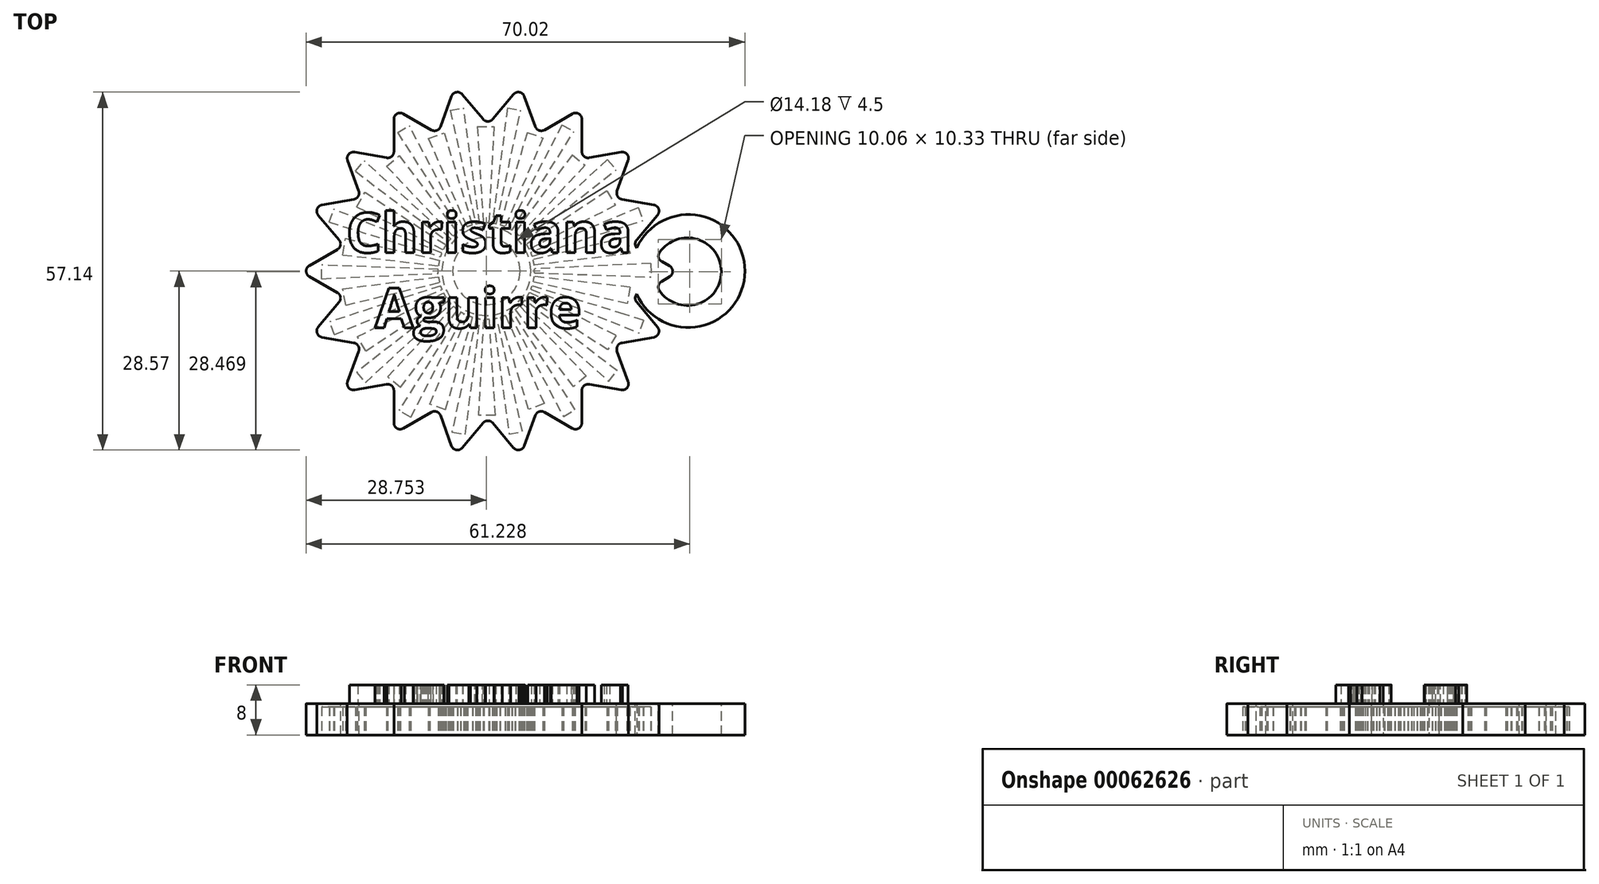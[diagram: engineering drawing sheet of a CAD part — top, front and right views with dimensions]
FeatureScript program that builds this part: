
annotation { "Feature Type Name" : "Feature", "Feature Type Description" : "" }
export const myFeature = defineFeature(function(context is Context, id is Id, definition is map)
    precondition{}
    {
        {
            var Q0;
            Q0=qCreatedBy(makeId("Top.planeOp"),FACE);
            var sketch = newSketch(context, id + "F0", { "sketchPlane" : qUnion([Q0])});
            skLineSegment(sketch, "E0", {"start": v(-64.22, 4.05) * mm, "end": v(-69.43, 10.26) * mm});
            skLineSegment(sketch, "E1", {"start": v(-69.43, 10.26) * mm, "end": v(-61.45, 11.67) * mm});
            skCircle(sketch, "E2.0", {"center": v(-41.24, 0) * mm, "radius": 30 * mm, "construction": true});
            skLineSegment(sketch, "E3", {"start": v(-61.45, 11.67) * mm, "end": v(-64.22, 19.28) * mm});
            skLineSegment(sketch, "E4", {"start": v(-64.22, 19.28) * mm, "end": v(-56.24, 17.88) * mm});
            skLineSegment(sketch, "E5", {"start": v(-56.24, 17.88) * mm, "end": v(-56.24, 25.98) * mm});
            skLineSegment(sketch, "E6", {"start": v(-56.24, 25.98) * mm, "end": v(-49.22, 21.93) * mm});
            skLineSegment(sketch, "E7", {"start": v(-49.22, 21.93) * mm, "end": v(-46.45, 29.54) * mm});
            skLineSegment(sketch, "E8", {"start": v(-46.45, 29.54) * mm, "end": v(-41.24, 23.34) * mm});
            skLineSegment(sketch, "E9", {"start": v(-41.24, 23.34) * mm, "end": v(-36.03, 29.54) * mm});
            skLineSegment(sketch, "E10", {"start": v(-36.03, 29.54) * mm, "end": v(-33.26, 21.93) * mm});
            skLineSegment(sketch, "E11", {"start": v(-33.26, 21.93) * mm, "end": v(-26.24, 25.98) * mm});
            skLineSegment(sketch, "E12", {"start": v(-26.24, 25.98) * mm, "end": v(-26.24, 17.88) * mm});
            skLineSegment(sketch, "E13", {"start": v(-26.24, 17.88) * mm, "end": v(-18.26, 19.28) * mm});
            skLineSegment(sketch, "E14", {"start": v(-18.26, 19.28) * mm, "end": v(-21.03, 11.67) * mm});
            skLineSegment(sketch, "E15", {"start": v(-21.03, 11.67) * mm, "end": v(-13.05, 10.26) * mm});
            skLineSegment(sketch, "E16", {"start": v(-13.05, 10.26) * mm, "end": v(-18.26, 4.05) * mm});
            skLineSegment(sketch, "E17", {"start": v(-18.26, 4.05) * mm, "end": v(-11.24, 0) * mm});
            skLineSegment(sketch, "E18", {"start": v(-11.24, 0) * mm, "end": v(-18.26, -4.05) * mm});
            skLineSegment(sketch, "E19", {"start": v(-18.26, -4.05) * mm, "end": v(-13.05, -10.26) * mm});
            skLineSegment(sketch, "E20", {"start": v(-13.05, -10.26) * mm, "end": v(-21.03, -11.67) * mm});
            skLineSegment(sketch, "E21", {"start": v(-21.03, -11.67) * mm, "end": v(-18.26, -19.28) * mm});
            skLineSegment(sketch, "E22", {"start": v(-18.26, -19.28) * mm, "end": v(-26.24, -17.88) * mm});
            skLineSegment(sketch, "E23", {"start": v(-26.24, -17.88) * mm, "end": v(-26.24, -25.98) * mm});
            skLineSegment(sketch, "E24", {"start": v(-26.24, -25.98) * mm, "end": v(-33.26, -21.93) * mm});
            skLineSegment(sketch, "E25", {"start": v(-33.26, -21.93) * mm, "end": v(-36.03, -29.54) * mm});
            skLineSegment(sketch, "E26", {"start": v(-46.45, -29.54) * mm, "end": v(-49.22, -21.93) * mm});
            skLineSegment(sketch, "E27", {"start": v(-49.22, -21.93) * mm, "end": v(-56.24, -25.98) * mm});
            skLineSegment(sketch, "E28", {"start": v(-56.24, -25.98) * mm, "end": v(-56.24, -17.88) * mm});
            skLineSegment(sketch, "E29", {"start": v(-56.24, -17.88) * mm, "end": v(-64.22, -19.28) * mm});
            skLineSegment(sketch, "E30", {"start": v(-64.22, -19.28) * mm, "end": v(-61.45, -11.67) * mm});
            skLineSegment(sketch, "E31", {"start": v(-61.45, -11.67) * mm, "end": v(-69.43, -10.26) * mm});
            skLineSegment(sketch, "E32", {"start": v(-69.43, -10.26) * mm, "end": v(-64.22, -4.05) * mm});
            skLineSegment(sketch, "E33", {"start": v(-64.22, -4.05) * mm, "end": v(-71.24, 0) * mm});
            skLineSegment(sketch, "E34", {"start": v(-71.24, 0) * mm, "end": v(-64.22, 4.05) * mm});
            skLineSegment(sketch, "E35", {"start": v(-46.45, -29.54) * mm, "end": v(-41.24, -23.34) * mm});
            skLineSegment(sketch, "E36", {"start": v(-41.24, -23.34) * mm, "end": v(-36.03, -29.54) * mm});
            skSolve(sketch);
        }
        {
            var Q0;
            Q0=qSketchRegion(id+"F0",true);
            extrude(context, id + "F1", {"entities" : qUnion([Q0]), "depth" : 5 * mm});
        }
        {
            var Q0;
            Q0=makeQuery(id+"F1.opExtrude","SWEPT_EDGE",EDGE,{"disambiguationData":[OSD([sQuery(id+"F0.wireOp",EDGE,"E26"),sQuery(id+"F0.wireOp",EDGE,"E27")])]});
            var Q1;
            Q1=makeQuery(id+"F1.opExtrude","SWEPT_EDGE",EDGE,{"disambiguationData":[OSD([sQuery(id+"F0.wireOp",EDGE,"E28"),sQuery(id+"F0.wireOp",EDGE,"E29")])]});
            var Q2;
            Q2=makeQuery(id+"F1.opExtrude","SWEPT_EDGE",EDGE,{"disambiguationData":[OSD([sQuery(id+"F0.wireOp",EDGE,"E30"),sQuery(id+"F0.wireOp",EDGE,"E31")])]});
            var Q3;
            Q3=makeQuery(id+"F1.opExtrude","SWEPT_EDGE",EDGE,{"disambiguationData":[OSD([sQuery(id+"F0.wireOp",EDGE,"E32"),sQuery(id+"F0.wireOp",EDGE,"E33")])]});
            var Q4;
            Q4=makeQuery(id+"F1.opExtrude","SWEPT_EDGE",EDGE,{"disambiguationData":[OSD([sQuery(id+"F0.wireOp",EDGE,"E0"),sQuery(id+"F0.wireOp",EDGE,"E34")])]});
            var Q5;
            Q5=makeQuery(id+"F1.opExtrude","SWEPT_EDGE",EDGE,{"disambiguationData":[OSD([sQuery(id+"F0.wireOp",EDGE,"E1"),sQuery(id+"F0.wireOp",EDGE,"E3")])]});
            var Q6;
            Q6=makeQuery(id+"F1.opExtrude","SWEPT_EDGE",EDGE,{"disambiguationData":[OSD([sQuery(id+"F0.wireOp",EDGE,"E4"),sQuery(id+"F0.wireOp",EDGE,"E5")])]});
            var Q7;
            Q7=makeQuery(id+"F1.opExtrude","SWEPT_EDGE",EDGE,{"disambiguationData":[OSD([sQuery(id+"F0.wireOp",EDGE,"E6"),sQuery(id+"F0.wireOp",EDGE,"E7")])]});
            var Q8;
            Q8=makeQuery(id+"F1.opExtrude","SWEPT_EDGE",EDGE,{"disambiguationData":[OSD([sQuery(id+"F0.wireOp",EDGE,"E8"),sQuery(id+"F0.wireOp",EDGE,"E9")])]});
            var Q9;
            Q9=makeQuery(id+"F1.opExtrude","SWEPT_EDGE",EDGE,{"disambiguationData":[OSD([sQuery(id+"F0.wireOp",EDGE,"E10"),sQuery(id+"F0.wireOp",EDGE,"E11")])]});
            var Q10;
            Q10=makeQuery(id+"F1.opExtrude","SWEPT_EDGE",EDGE,{"disambiguationData":[OSD([sQuery(id+"F0.wireOp",EDGE,"E35"),sQuery(id+"F0.wireOp",EDGE,"E36")])]});
            var Q11;
            Q11=makeQuery(id+"F1.opExtrude","SWEPT_EDGE",EDGE,{"disambiguationData":[OSD([sQuery(id+"F0.wireOp",EDGE,"E24"),sQuery(id+"F0.wireOp",EDGE,"E25")])]});
            var Q12;
            Q12=makeQuery(id+"F1.opExtrude","SWEPT_EDGE",EDGE,{"disambiguationData":[OSD([sQuery(id+"F0.wireOp",EDGE,"E22"),sQuery(id+"F0.wireOp",EDGE,"E23")])]});
            var Q13;
            Q13=makeQuery(id+"F1.opExtrude","SWEPT_EDGE",EDGE,{"disambiguationData":[OSD([sQuery(id+"F0.wireOp",EDGE,"E20"),sQuery(id+"F0.wireOp",EDGE,"E21")])]});
            var Q14;
            Q14=makeQuery(id+"F1.opExtrude","SWEPT_EDGE",EDGE,{"disambiguationData":[OSD([sQuery(id+"F0.wireOp",EDGE,"E12"),sQuery(id+"F0.wireOp",EDGE,"E13")])]});
            var Q15;
            Q15=makeQuery(id+"F1.opExtrude","SWEPT_EDGE",EDGE,{"disambiguationData":[OSD([sQuery(id+"F0.wireOp",EDGE,"E14"),sQuery(id+"F0.wireOp",EDGE,"E15")])]});
            var Q16;
            Q16=makeQuery(id+"F1.opExtrude","SWEPT_EDGE",EDGE,{"disambiguationData":[OSD([sQuery(id+"F0.wireOp",EDGE,"E16"),sQuery(id+"F0.wireOp",EDGE,"E17")])]});
            var Q17;
            Q17=makeQuery(id+"F1.opExtrude","SWEPT_EDGE",EDGE,{"disambiguationData":[OSD([sQuery(id+"F0.wireOp",EDGE,"E18"),sQuery(id+"F0.wireOp",EDGE,"E19")])]});
            fillet(context, id + "F2", {"entities" : qUnion([Q0, Q1, Q2, Q3, Q4, Q5, Q6, Q7, Q8, Q9, Q10, Q11, Q12, Q13, Q14, Q15, Q16, Q17]), "radius" : 1 * mm, "tangentPropagation" : true, "allowEdgeOverflow" : false});
        }
        {
            var Q0;
            Q0=makeQuery(id+"F1.opExtrude","SWEPT_EDGE",EDGE,{"disambiguationData":[OSD([sQuery(id+"F0.wireOp",EDGE,"E9"),sQuery(id+"F0.wireOp",EDGE,"E10")])]});
            var Q1;
            Q1=makeQuery(id+"F1.opExtrude","SWEPT_EDGE",EDGE,{"disambiguationData":[OSD([sQuery(id+"F0.wireOp",EDGE,"E11"),sQuery(id+"F0.wireOp",EDGE,"E12")])]});
            var Q2;
            Q2=makeQuery(id+"F1.opExtrude","SWEPT_EDGE",EDGE,{"disambiguationData":[OSD([sQuery(id+"F0.wireOp",EDGE,"E13"),sQuery(id+"F0.wireOp",EDGE,"E14")])]});
            var Q3;
            Q3=makeQuery(id+"F1.opExtrude","SWEPT_EDGE",EDGE,{"disambiguationData":[OSD([sQuery(id+"F0.wireOp",EDGE,"E15"),sQuery(id+"F0.wireOp",EDGE,"E16")])]});
            var Q4;
            Q4=makeQuery(id+"F1.opExtrude","SWEPT_EDGE",EDGE,{"disambiguationData":[OSD([sQuery(id+"F0.wireOp",EDGE,"E17"),sQuery(id+"F0.wireOp",EDGE,"E18")])]});
            var Q5;
            Q5=makeQuery(id+"F1.opExtrude","SWEPT_EDGE",EDGE,{"disambiguationData":[OSD([sQuery(id+"F0.wireOp",EDGE,"E19"),sQuery(id+"F0.wireOp",EDGE,"E20")])]});
            var Q6;
            Q6=makeQuery(id+"F1.opExtrude","SWEPT_EDGE",EDGE,{"disambiguationData":[OSD([sQuery(id+"F0.wireOp",EDGE,"E5"),sQuery(id+"F0.wireOp",EDGE,"E6")])]});
            var Q7;
            Q7=makeQuery(id+"F1.opExtrude","SWEPT_EDGE",EDGE,{"disambiguationData":[OSD([sQuery(id+"F0.wireOp",EDGE,"E7"),sQuery(id+"F0.wireOp",EDGE,"E8")])]});
            var Q8;
            Q8=makeQuery(id+"F1.opExtrude","SWEPT_EDGE",EDGE,{"disambiguationData":[OSD([sQuery(id+"F0.wireOp",EDGE,"E3"),sQuery(id+"F0.wireOp",EDGE,"E4")])]});
            var Q9;
            Q9=makeQuery(id+"F1.opExtrude","SWEPT_EDGE",EDGE,{"disambiguationData":[OSD([sQuery(id+"F0.wireOp",EDGE,"E0"),sQuery(id+"F0.wireOp",EDGE,"E1")])]});
            var Q10;
            Q10=makeQuery(id+"F1.opExtrude","SWEPT_EDGE",EDGE,{"disambiguationData":[OSD([sQuery(id+"F0.wireOp",EDGE,"E33"),sQuery(id+"F0.wireOp",EDGE,"E34")])]});
            var Q11;
            Q11=makeQuery(id+"F1.opExtrude","SWEPT_EDGE",EDGE,{"disambiguationData":[OSD([sQuery(id+"F0.wireOp",EDGE,"E31"),sQuery(id+"F0.wireOp",EDGE,"E32")])]});
            var Q12;
            Q12=makeQuery(id+"F1.opExtrude","SWEPT_EDGE",EDGE,{"disambiguationData":[OSD([sQuery(id+"F0.wireOp",EDGE,"E29"),sQuery(id+"F0.wireOp",EDGE,"E30")])]});
            var Q13;
            Q13=makeQuery(id+"F1.opExtrude","SWEPT_EDGE",EDGE,{"disambiguationData":[OSD([sQuery(id+"F0.wireOp",EDGE,"E27"),sQuery(id+"F0.wireOp",EDGE,"E28")])]});
            var Q14;
            Q14=makeQuery(id+"F1.opExtrude","SWEPT_EDGE",EDGE,{"disambiguationData":[OSD([sQuery(id+"F0.wireOp",EDGE,"E26"),sQuery(id+"F0.wireOp",EDGE,"E35")])]});
            var Q15;
            Q15=makeQuery(id+"F1.opExtrude","SWEPT_EDGE",EDGE,{"disambiguationData":[OSD([sQuery(id+"F0.wireOp",EDGE,"E25"),sQuery(id+"F0.wireOp",EDGE,"E36")])]});
            var Q16;
            Q16=makeQuery(id+"F1.opExtrude","SWEPT_EDGE",EDGE,{"disambiguationData":[OSD([sQuery(id+"F0.wireOp",EDGE,"E23"),sQuery(id+"F0.wireOp",EDGE,"E24")])]});
            var Q17;
            Q17=makeQuery(id+"F1.opExtrude","SWEPT_EDGE",EDGE,{"disambiguationData":[OSD([sQuery(id+"F0.wireOp",EDGE,"E21"),sQuery(id+"F0.wireOp",EDGE,"E22")])]});
            fillet(context, id + "F3", {"entities" : qUnion([Q0, Q1, Q2, Q3, Q4, Q5, Q6, Q7, Q8, Q9, Q10, Q11, Q12, Q13, Q14, Q15, Q16, Q17]), "radius" : 1 * mm, "tangentPropagation" : true, "allowEdgeOverflow" : false});
        }
        {
            var Q0;
            Q0=qCreatedBy(makeId("Top.planeOp"),FACE);
            var sketch = newSketch(context, id + "F4", { "sketchPlane" : qUnion([Q0])});
            skCircle(sketch, "E37", {"center": v(-9.24, 0) * mm, "radius": 9.02 * mm});
            skSolve(sketch);
        }
        {
            var Q0;
            Q0=qSketchRegion(id+"F4",true);
            var Q1;
            {var subQ0=sQuery(id+"F0.wireOp",EDGE,"E30");var subQ1=sQuery(id+"F0.wireOp",EDGE,"E16");var subQ2=sQuery(id+"F0.wireOp",EDGE,"E31");var subQ3=sQuery(id+"F0.wireOp",EDGE,"E27");var subQ4=sQuery(id+"F0.wireOp",EDGE,"E23");var subQ5=sQuery(id+"F0.wireOp",EDGE,"E21");var subQ6=sQuery(id+"F0.wireOp",EDGE,"E13");var subQ7=sQuery(id+"F0.wireOp",EDGE,"E14");var subQ8=sQuery(id+"F0.wireOp",EDGE,"E20");var subQ9=sQuery(id+"F0.wireOp",EDGE,"E22");var subQ10=sQuery(id+"F0.wireOp",EDGE,"E19");var subQ11=sQuery(id+"F0.wireOp",EDGE,"E11");var subQ12=sQuery(id+"F0.wireOp",EDGE,"E18");var subQ13=sQuery(id+"F0.wireOp",EDGE,"E17");var subQ14=sQuery(id+"F0.wireOp",EDGE,"E12");var subQ15=sQuery(id+"F0.wireOp",EDGE,"E4");var subQ16=sQuery(id+"F0.wireOp",EDGE,"E3");var subQ17=sQuery(id+"F0.wireOp",EDGE,"E32");var subQ18=sQuery(id+"F0.wireOp",EDGE,"E1");var subQ19=sQuery(id+"F0.wireOp",EDGE,"E9");var subQ20=sQuery(id+"F0.wireOp",EDGE,"E0");var subQ21=sQuery(id+"F0.wireOp",EDGE,"E5");var subQ22=sQuery(id+"F0.wireOp",EDGE,"E6");var subQ23=sQuery(id+"F0.wireOp",EDGE,"E7");var subQ24=sQuery(id+"F0.wireOp",EDGE,"E36");var subQ25=sQuery(id+"F0.wireOp",EDGE,"E15");var subQ26=sQuery(id+"F0.wireOp",EDGE,"E8");var subQ27=sQuery(id+"F0.wireOp",EDGE,"E34");var subQ28=sQuery(id+"F0.wireOp",EDGE,"E25");var subQ29=sQuery(id+"F0.wireOp",EDGE,"E29");var subQ30=sQuery(id+"F0.wireOp",EDGE,"E26");var subQ31=sQuery(id+"F0.wireOp",EDGE,"E35");var subQ32=sQuery(id+"F0.wireOp",EDGE,"E33");var subQ33=sQuery(id+"F0.wireOp",EDGE,"E24");var subQ34=sQuery(id+"F0.wireOp",EDGE,"E10");var subQ35=sQuery(id+"F0.wireOp",EDGE,"E28");Q1=makeQuery(id+"FIdaEZY0NoQjCEp_1.boolean.opBoolean","SPLIT",FACE,{"disambiguationData":[TD([makeQuery(id+"F1.opExtrude","SWEPT_FACE",FACE,{"disambiguationData":[OSD([subQ20])]})])],"derivedFrom":makeQuery(id+"F1.opExtrude","CAP_FACE",FACE,{"disambiguationData":[OSD([subQ20,subQ18,subQ16,subQ15,subQ21,subQ22,subQ23,subQ26,subQ19,subQ34,subQ11,subQ14,subQ6,subQ7,subQ25,subQ1,subQ13,subQ12,subQ10,subQ8,subQ5,subQ9,subQ4,subQ33,subQ28,subQ30,subQ3,subQ35,subQ29,subQ0,subQ2,subQ17,subQ32,subQ27,subQ31,subQ24])],"isStart":false})});}
            extrude(context, id + "F5", {"entities" : qUnion([Q0]), "operationType" : NewBodyOperationType.ADD, "endBound" : BoundingType.UP_TO_SURFACE, "endBoundEntityFace" : qUnion([Q1]), "depth" : 25 * mm});
        }
        {
            var Q0;
            {var subQ0=sQuery(id+"F0.wireOp",EDGE,"E36");var subQ1=sQuery(id+"F0.wireOp",EDGE,"E35");var subQ2=sQuery(id+"F0.wireOp",EDGE,"E34");var subQ3=sQuery(id+"F0.wireOp",EDGE,"E33");var subQ4=sQuery(id+"F0.wireOp",EDGE,"E32");var subQ5=sQuery(id+"F0.wireOp",EDGE,"E31");var subQ6=sQuery(id+"F0.wireOp",EDGE,"E30");var subQ7=sQuery(id+"F0.wireOp",EDGE,"E29");var subQ8=sQuery(id+"F0.wireOp",EDGE,"E28");var subQ9=sQuery(id+"F0.wireOp",EDGE,"E27");var subQ10=sQuery(id+"F0.wireOp",EDGE,"E26");var subQ11=sQuery(id+"F0.wireOp",EDGE,"E25");var subQ12=sQuery(id+"F0.wireOp",EDGE,"E24");var subQ13=sQuery(id+"F0.wireOp",EDGE,"E23");var subQ14=sQuery(id+"F0.wireOp",EDGE,"E22");var subQ15=sQuery(id+"F0.wireOp",EDGE,"E21");var subQ16=sQuery(id+"F0.wireOp",EDGE,"E20");var subQ17=sQuery(id+"F0.wireOp",EDGE,"E19");var subQ18=sQuery(id+"F0.wireOp",EDGE,"E18");var subQ19=sQuery(id+"F0.wireOp",EDGE,"E17");var subQ20=sQuery(id+"F0.wireOp",EDGE,"E16");var subQ21=sQuery(id+"F0.wireOp",EDGE,"E15");var subQ22=sQuery(id+"F0.wireOp",EDGE,"E14");var subQ23=sQuery(id+"F0.wireOp",EDGE,"E13");var subQ24=sQuery(id+"F0.wireOp",EDGE,"E12");var subQ25=sQuery(id+"F0.wireOp",EDGE,"E11");var subQ26=sQuery(id+"F0.wireOp",EDGE,"E10");var subQ27=sQuery(id+"F0.wireOp",EDGE,"E9");var subQ28=sQuery(id+"F0.wireOp",EDGE,"E8");var subQ29=sQuery(id+"F0.wireOp",EDGE,"E7");var subQ30=sQuery(id+"F0.wireOp",EDGE,"E6");var subQ31=sQuery(id+"F0.wireOp",EDGE,"E5");var subQ32=sQuery(id+"F0.wireOp",EDGE,"E4");var subQ33=sQuery(id+"F0.wireOp",EDGE,"E3");var subQ34=sQuery(id+"F0.wireOp",EDGE,"E1");var subQ35=sQuery(id+"F0.wireOp",EDGE,"E0");Q0=makeQuery(id+"F5.boolean.opBoolean","MERGE",FACE,{"derivedFrom":[makeQuery(id+"F1.opExtrude","CAP_FACE",FACE,{"disambiguationData":[OSD([subQ35,subQ34,subQ33,subQ32,subQ31,subQ30,subQ29,subQ28,subQ27,subQ26,subQ25,subQ24,subQ23,subQ22,subQ21,subQ20,subQ19,subQ18,subQ17,subQ16,subQ15,subQ14,subQ13,subQ12,subQ11,subQ10,subQ9,subQ8,subQ7,subQ6,subQ5,subQ4,subQ3,subQ2,subQ1,subQ0])],"isStart":false}),makeQuery(id+"F5.opExtrude","CAP_FACE",FACE,{"disambiguationData":[OSD([subQ35,subQ34,subQ33,subQ32,subQ31,subQ30,subQ29,subQ28,subQ27,subQ26,subQ25,subQ24,subQ23,subQ22,subQ21,subQ20,subQ19,subQ18,subQ17,subQ16,subQ15,subQ14,subQ13,subQ12,subQ11,subQ10,subQ9,subQ8,subQ7,subQ6,subQ5,subQ4,subQ3,subQ2,subQ1,subQ0])],"isStart":false})]});}
            var sketch = newSketch(context, id + "F6", { "sketchPlane" : qUnion([Q0])});
            skLineSegment(sketch, "E38", {"start": v(-14.37, 2) * mm, "end": v(-10.75, 0) * mm});
            skLineSegment(sketch, "E39", {"start": v(-10.75, 0) * mm, "end": v(-14.37, -2.19) * mm});
            skArc(sketch, "E40", {"start": v(-14.37, -2.19) * mm, "mid": v(-3.98, -0.1) * mm, "end": v(-14.37, 2) * mm});
            skSolve(sketch);
        }
        {
            var Q0;
            Q0=qSketchRegion(id+"F6",true);
            var Q1;
            Q1=makeQuery(id+"F5.boolean.opBoolean","MERGE",FACE,{"derivedFrom":[makeQuery(id+"F1.opExtrude","CAP_FACE",FACE,{"disambiguationData":[OSD([sQuery(id+"F0.wireOp",EDGE,"E0"),sQuery(id+"F0.wireOp",EDGE,"E1"),sQuery(id+"F0.wireOp",EDGE,"E3"),sQuery(id+"F0.wireOp",EDGE,"E4"),sQuery(id+"F0.wireOp",EDGE,"E5"),sQuery(id+"F0.wireOp",EDGE,"E6"),sQuery(id+"F0.wireOp",EDGE,"E7"),sQuery(id+"F0.wireOp",EDGE,"E8"),sQuery(id+"F0.wireOp",EDGE,"E9"),sQuery(id+"F0.wireOp",EDGE,"E10"),sQuery(id+"F0.wireOp",EDGE,"E11"),sQuery(id+"F0.wireOp",EDGE,"E12"),sQuery(id+"F0.wireOp",EDGE,"E13"),sQuery(id+"F0.wireOp",EDGE,"E14"),sQuery(id+"F0.wireOp",EDGE,"E15"),sQuery(id+"F0.wireOp",EDGE,"E16"),sQuery(id+"F0.wireOp",EDGE,"E17"),sQuery(id+"F0.wireOp",EDGE,"E18"),sQuery(id+"F0.wireOp",EDGE,"E19"),sQuery(id+"F0.wireOp",EDGE,"E20"),sQuery(id+"F0.wireOp",EDGE,"E21"),sQuery(id+"F0.wireOp",EDGE,"E22"),sQuery(id+"F0.wireOp",EDGE,"E23"),sQuery(id+"F0.wireOp",EDGE,"E24"),sQuery(id+"F0.wireOp",EDGE,"E25"),sQuery(id+"F0.wireOp",EDGE,"E26"),sQuery(id+"F0.wireOp",EDGE,"E27"),sQuery(id+"F0.wireOp",EDGE,"E28"),sQuery(id+"F0.wireOp",EDGE,"E29"),sQuery(id+"F0.wireOp",EDGE,"E30"),sQuery(id+"F0.wireOp",EDGE,"E31"),sQuery(id+"F0.wireOp",EDGE,"E32"),sQuery(id+"F0.wireOp",EDGE,"E33"),sQuery(id+"F0.wireOp",EDGE,"E34"),sQuery(id+"F0.wireOp",EDGE,"E35"),sQuery(id+"F0.wireOp",EDGE,"E36")])],"isStart":true}),makeQuery(id+"F5.opExtrude","CAP_FACE",FACE,{"disambiguationData":[OSD([sQuery(id+"F4.wireOp",EDGE,"E37")])],"isStart":true})]});
            extrude(context, id + "F7", {"entities" : qUnion([Q0]), "operationType" : NewBodyOperationType.REMOVE, "endBound" : BoundingType.UP_TO_SURFACE, "oppositeDirection" : true, "endBoundEntityFace" : qUnion([Q1]), "depth" : 25 * mm});
        }
        {
            var Q0;
            Q0=makeQuery(id+"F7.boolean.opBoolean","COPY",EDGE,{"derivedFrom":makeQuery(id+"F7.opExtrude","SWEPT_EDGE",EDGE,{"disambiguationData":[OSD([sQuery(id+"F6.wireOp",EDGE,"KMGjyx1H-Efwy-Ger7-KHIj-FZDtgPy88TKw"),sQuery(id+"F6.wireOp",EDGE,"Em1Z4o3I-NRpS-VtHU-MFej-VVcVSapDzxZl")])]})});
            var Q1;
            Q1=makeQuery(id+"F7.boolean.opBoolean","COPY",EDGE,{"derivedFrom":makeQuery(id+"F7.opExtrude","SWEPT_EDGE",EDGE,{"disambiguationData":[OSD([sQuery(id+"F6.wireOp",EDGE,"E38"),sQuery(id+"F6.wireOp",EDGE,"E39")])]})});
            var Q2;
            Q2=makeQuery(id+"F7.boolean.opBoolean","COPY",EDGE,{"derivedFrom":makeQuery(id+"F7.opExtrude","SWEPT_EDGE",EDGE,{"disambiguationData":[OSD([sQuery(id+"F6.wireOp",EDGE,"E39"),sQuery(id+"F6.wireOp",EDGE,"E40")])]})});
            var Q3;
            Q3=makeQuery(id+"F7.boolean.opBoolean","COPY",EDGE,{"derivedFrom":makeQuery(id+"F7.opExtrude","SWEPT_EDGE",EDGE,{"disambiguationData":[OSD([sQuery(id+"F6.wireOp",EDGE,"E38"),sQuery(id+"F6.wireOp",EDGE,"E40")])]})});
            fillet(context, id + "F8", {"entities" : qUnion([Q0, Q1, Q2, Q3]), "radius" : 1 * mm, "tangentPropagation" : true, "allowEdgeOverflow" : false});
        }
        {
            var Q0;
            Q0=makeQuery(id+"F0.imprint","IMPRINT",FACE,{"disambiguationData":[TD([[makeQuery(id+"F0.imprint","IMPRINT",EDGE,{"derivedFrom":sQuery(id+"F0.wireOp",EDGE,"E0")}),-1.0]])]});
            var sketch = newSketch(context, id + "F9", { "sketchPlane" : qUnion([Q0])});
            skCircle(sketch, "E41", {"center": v(-41.49, 0) * mm, "radius": 26.28 * mm, "construction": true});
            skCircle(sketch, "E42", {"center": v(-41.49, 0) * mm, "radius": 23.08 * mm, "construction": true});
            skLineSegment(sketch, "E43", {"start": v(-41.49, 0) * mm, "end": v(-21.98, -17.6) * mm, "construction": true});
            skLineSegment(sketch, "E44", {"start": v(-21.98, -17.6) * mm, "end": v(-20.6, -15.94) * mm, "construction": true});
            skLineSegment(sketch, "E45", {"start": v(-20.6, -15.94) * mm, "end": v(-41.49, 0) * mm, "construction": true});
            skLineSegment(sketch, "E46", {"start": v(-41.49, 0) * mm, "end": v(-22.13, -12.57) * mm, "construction": true});
            skLineSegment(sketch, "E47", {"start": v(-22.13, -12.57) * mm, "end": v(-20.8, -10.26) * mm, "construction": true});
            skLineSegment(sketch, "E48", {"start": v(-20.8, -10.26) * mm, "end": v(-41.49, 0) * mm, "construction": true});
            skLineSegment(sketch, "E49", {"start": v(-41.49, 0) * mm, "end": v(-21.03, -11.67) * mm, "construction": true});
            skLineSegment(sketch, "E50", {"start": v(-41.49, 0) * mm, "end": v(-18.26, -19.28) * mm, "construction": true});
            skLineSegment(sketch, "E51", {"start": v(-20.8, -10.26) * mm, "end": v(-21.03, -11.67) * mm, "construction": true});
            skLineSegment(sketch, "E52", {"start": v(-22.13, -12.57) * mm, "end": v(-21.03, -11.67) * mm, "construction": true});
            skLineSegment(sketch, "E53", {"start": v(-18.26, -19.28) * mm, "end": v(-21.98, -17.6) * mm, "construction": true});
            skLineSegment(sketch, "E54", {"start": v(-20.6, -15.94) * mm, "end": v(-18.26, -19.28) * mm, "construction": true});
            skLineSegment(sketch, "E55", {"start": v(-35.78, -5.15) * mm, "end": v(-21.98, -17.6) * mm});
            skLineSegment(sketch, "E56", {"start": v(-20.6, -15.94) * mm, "end": v(-35.38, -4.66) * mm});
            skLineSegment(sketch, "E57", {"start": v(-22.13, -12.57) * mm, "end": v(-35.04, -4.18) * mm});
            skLineSegment(sketch, "E58", {"start": v(-20.8, -10.26) * mm, "end": v(-22.13, -12.57) * mm});
            skLineSegment(sketch, "E59", {"start": v(-20.8, -10.26) * mm, "end": v(-34.6, -3.42) * mm});
            skLineSegment(sketch, "E60.1.0", {"start": v(-34.37, -2.89) * mm, "end": v(-17.13, -9.87) * mm});
            skLineSegment(sketch, "E60.1.1", {"start": v(-17.13, -9.87) * mm, "end": v(-16.4, -7.83) * mm, "construction": true});
            skLineSegment(sketch, "E60.1.2", {"start": v(-16.4, -7.83) * mm, "end": v(-19.45, -6.88) * mm});
            skLineSegment(sketch, "E60.1.3", {"start": v(-19, -5.2) * mm, "end": v(-34, -1.73) * mm});
            skLineSegment(sketch, "E60.1.4", {"start": v(-18.55, -2.57) * mm, "end": v(-19, -5.2) * mm});
            skLineSegment(sketch, "E60.1.5", {"start": v(-18.55, -2.57) * mm, "end": v(-33.85, -0.86) * mm});
            skLineSegment(sketch, "E60.2.0", {"start": v(-33.8, -0.28) * mm, "end": v(-15.22, -0.95) * mm});
            skLineSegment(sketch, "E60.2.1", {"start": v(-15.22, -0.95) * mm, "end": v(-15.23, 1.22) * mm, "construction": true});
            skLineSegment(sketch, "E60.2.2", {"start": v(-15.23, 1.22) * mm, "end": v(-33.81, 0.36) * mm});
            skLineSegment(sketch, "E60.2.3", {"start": v(-18.57, 2.81) * mm, "end": v(-33.86, 0.94) * mm});
            skLineSegment(sketch, "E60.2.4", {"start": v(-19.05, 5.43) * mm, "end": v(-18.57, 2.81) * mm});
            skLineSegment(sketch, "E60.2.5", {"start": v(-19.05, 5.43) * mm, "end": v(-34.02, 1.8) * mm});
            skLineSegment(sketch, "E60.3.0", {"start": v(-34.18, 2.37) * mm, "end": v(-16.48, 8.1) * mm});
            skLineSegment(sketch, "E60.3.1", {"start": v(-16.48, 8.1) * mm, "end": v(-17.23, 10.13) * mm, "construction": true});
            skLineSegment(sketch, "E60.3.2", {"start": v(-17.23, 10.13) * mm, "end": v(-34.4, 2.96) * mm});
            skLineSegment(sketch, "E60.3.3", {"start": v(-20.92, 10.48) * mm, "end": v(-34.64, 3.49) * mm});
            skLineSegment(sketch, "E60.3.4", {"start": v(-22.26, 12.78) * mm, "end": v(-20.92, 10.48) * mm});
            skLineSegment(sketch, "E60.3.5", {"start": v(-22.26, 12.78) * mm, "end": v(-35.09, 4.25) * mm});
            skLineSegment(sketch, "E60.4.0", {"start": v(-35.43, 4.72) * mm, "end": v(-20.76, 16.16) * mm});
            skLineSegment(sketch, "E60.4.1", {"start": v(-20.76, 16.16) * mm, "end": v(-22.16, 17.81) * mm, "construction": true});
            skLineSegment(sketch, "E60.4.2", {"start": v(-22.16, 17.81) * mm, "end": v(-35.84, 5.2) * mm});
            skLineSegment(sketch, "E60.4.3", {"start": v(-25.74, 16.88) * mm, "end": v(-36.25, 5.62) * mm});
            skLineSegment(sketch, "E60.4.4", {"start": v(-27.79, 18.58) * mm, "end": v(-25.74, 16.88) * mm});
            skLineSegment(sketch, "E60.4.5", {"start": v(-27.79, 18.58) * mm, "end": v(-36.93, 6.18) * mm});
            skLineSegment(sketch, "E60.5.0", {"start": v(-37.4, 6.51) * mm, "end": v(-27.53, 22.27) * mm});
            skLineSegment(sketch, "E60.5.1", {"start": v(-27.53, 22.27) * mm, "end": v(-29.42, 23.35) * mm, "construction": true});
            skLineSegment(sketch, "E60.5.2", {"start": v(-29.42, 23.35) * mm, "end": v(-37.96, 6.83) * mm});
            skLineSegment(sketch, "E60.5.3", {"start": v(-32.47, 21.25) * mm, "end": v(-38.48, 7.07) * mm});
            skLineSegment(sketch, "E60.5.4", {"start": v(-34.97, 22.15) * mm, "end": v(-32.47, 21.25) * mm});
            skLineSegment(sketch, "E60.5.5", {"start": v(-34.97, 22.15) * mm, "end": v(-39.32, 7.37) * mm});
            skLineSegment(sketch, "E60.6.0", {"start": v(-39.88, 7.51) * mm, "end": v(-36, 25.7) * mm});
            skLineSegment(sketch, "E60.6.1", {"start": v(-36, 25.7) * mm, "end": v(-38.13, 26.07) * mm, "construction": true});
            skLineSegment(sketch, "E60.6.2", {"start": v(-38.13, 26.07) * mm, "end": v(-40.5, 7.62) * mm});
            skLineSegment(sketch, "E60.6.3", {"start": v(-40.28, 23.05) * mm, "end": v(-41.08, 7.67) * mm});
            skLineSegment(sketch, "E60.6.4", {"start": v(-42.94, 23.04) * mm, "end": v(-40.28, 23.05) * mm});
            skLineSegment(sketch, "E60.6.5", {"start": v(-42.94, 23.04) * mm, "end": v(-41.97, 7.67) * mm});
            skLineSegment(sketch, "E60.7.0", {"start": v(-42.55, 7.6) * mm, "end": v(-45.11, 26.03) * mm});
            skLineSegment(sketch, "E60.7.1", {"start": v(-45.11, 26.03) * mm, "end": v(-47.25, 25.64) * mm, "construction": true});
            skLineSegment(sketch, "E60.7.2", {"start": v(-47.25, 25.64) * mm, "end": v(-43.17, 7.5) * mm});
            skLineSegment(sketch, "E60.7.3", {"start": v(-48.24, 22.08) * mm, "end": v(-43.73, 7.35) * mm});
            skLineSegment(sketch, "E60.7.4", {"start": v(-50.73, 21.15) * mm, "end": v(-48.24, 22.08) * mm});
            skLineSegment(sketch, "E60.7.5", {"start": v(-50.73, 21.15) * mm, "end": v(-44.56, 7.04) * mm});
            skLineSegment(sketch, "E60.8.0", {"start": v(-45.09, 6.79) * mm, "end": v(-53.8, 23.22) * mm});
            skLineSegment(sketch, "E60.8.1", {"start": v(-53.8, 23.22) * mm, "end": v(-55.67, 22.13) * mm, "construction": true});
            skLineSegment(sketch, "E60.8.2", {"start": v(-55.67, 22.13) * mm, "end": v(-45.63, 6.47) * mm});
            skLineSegment(sketch, "E60.8.3", {"start": v(-55.38, 18.44) * mm, "end": v(-46.11, 6.14) * mm});
            skLineSegment(sketch, "E60.8.4", {"start": v(-57.4, 16.72) * mm, "end": v(-55.38, 18.44) * mm});
            skLineSegment(sketch, "E60.8.5", {"start": v(-57.4, 16.72) * mm, "end": v(-46.79, 5.56) * mm});
            skLineSegment(sketch, "E60.9.0", {"start": v(-47.2, 5.15) * mm, "end": v(-61, 17.6) * mm});
            skLineSegment(sketch, "E60.9.1", {"start": v(-61, 17.6) * mm, "end": v(-62.38, 15.94) * mm, "construction": true});
            skLineSegment(sketch, "E60.9.2", {"start": v(-62.38, 15.94) * mm, "end": v(-47.6, 4.66) * mm});
            skLineSegment(sketch, "E60.9.3", {"start": v(-60.85, 12.57) * mm, "end": v(-47.93, 4.18) * mm});
            skLineSegment(sketch, "E60.9.4", {"start": v(-62.16, 10.26) * mm, "end": v(-60.85, 12.57) * mm});
            skLineSegment(sketch, "E60.9.5", {"start": v(-62.16, 10.26) * mm, "end": v(-48.37, 3.42) * mm});
            skLineSegment(sketch, "E60.10.0", {"start": v(-48.6, 2.89) * mm, "end": v(-65.84, 9.87) * mm});
            skLineSegment(sketch, "E60.10.1", {"start": v(-65.84, 9.87) * mm, "end": v(-66.57, 7.83) * mm, "construction": true});
            skLineSegment(sketch, "E60.10.2", {"start": v(-66.57, 7.83) * mm, "end": v(-48.82, 2.29) * mm});
            skLineSegment(sketch, "E60.10.3", {"start": v(-63.98, 5.2) * mm, "end": v(-48.97, 1.73) * mm});
            skLineSegment(sketch, "E60.10.4", {"start": v(-64.43, 2.57) * mm, "end": v(-63.98, 5.2) * mm});
            skLineSegment(sketch, "E60.10.5", {"start": v(-64.43, 2.57) * mm, "end": v(-49.12, 0.86) * mm});
            skLineSegment(sketch, "E60.11.0", {"start": v(-49.17, 0.28) * mm, "end": v(-67.75, 0.95) * mm});
            skLineSegment(sketch, "E60.11.1", {"start": v(-67.75, 0.95) * mm, "end": v(-67.74, -1.22) * mm, "construction": true});
            skLineSegment(sketch, "E60.11.2", {"start": v(-67.74, -1.22) * mm, "end": v(-49.16, -0.36) * mm});
            skLineSegment(sketch, "E60.11.3", {"start": v(-64.4, -2.81) * mm, "end": v(-49.11, -0.94) * mm});
            skLineSegment(sketch, "E60.11.4", {"start": v(-63.92, -5.43) * mm, "end": v(-64.4, -2.81) * mm});
            skLineSegment(sketch, "E60.11.5", {"start": v(-63.92, -5.43) * mm, "end": v(-48.95, -1.8) * mm});
            skLineSegment(sketch, "E60.12.0", {"start": v(-48.8, -2.37) * mm, "end": v(-66.5, -8.1) * mm});
            skLineSegment(sketch, "E60.12.1", {"start": v(-66.5, -8.1) * mm, "end": v(-65.74, -10.13) * mm, "construction": true});
            skLineSegment(sketch, "E60.12.2", {"start": v(-65.74, -10.13) * mm, "end": v(-48.58, -2.96) * mm});
            skLineSegment(sketch, "E60.12.3", {"start": v(-62.06, -10.48) * mm, "end": v(-48.33, -3.49) * mm});
            skLineSegment(sketch, "E60.12.4", {"start": v(-60.71, -12.78) * mm, "end": v(-62.06, -10.48) * mm});
            skLineSegment(sketch, "E60.12.5", {"start": v(-60.71, -12.78) * mm, "end": v(-47.89, -4.25) * mm});
            skLineSegment(sketch, "E60.13.0", {"start": v(-47.55, -4.72) * mm, "end": v(-62.22, -16.16) * mm});
            skLineSegment(sketch, "E60.13.1", {"start": v(-62.22, -16.16) * mm, "end": v(-60.81, -17.81) * mm, "construction": true});
            skLineSegment(sketch, "E60.13.2", {"start": v(-60.81, -17.81) * mm, "end": v(-47.14, -5.2) * mm});
            skLineSegment(sketch, "E60.13.3", {"start": v(-57.23, -16.88) * mm, "end": v(-46.73, -5.62) * mm});
            skLineSegment(sketch, "E60.13.4", {"start": v(-55.18, -18.58) * mm, "end": v(-57.23, -16.88) * mm});
            skLineSegment(sketch, "E60.13.5", {"start": v(-55.18, -18.58) * mm, "end": v(-46.05, -6.18) * mm});
            skLineSegment(sketch, "E60.14.0", {"start": v(-45.57, -6.51) * mm, "end": v(-55.44, -22.27) * mm});
            skLineSegment(sketch, "E60.14.1", {"start": v(-55.44, -22.27) * mm, "end": v(-53.56, -23.35) * mm, "construction": true});
            skLineSegment(sketch, "E60.14.2", {"start": v(-53.56, -23.35) * mm, "end": v(-45.01, -6.83) * mm});
            skLineSegment(sketch, "E60.14.3", {"start": v(-50.5, -21.25) * mm, "end": v(-44.49, -7.07) * mm});
            skLineSegment(sketch, "E60.14.4", {"start": v(-48, -22.15) * mm, "end": v(-50.5, -21.25) * mm});
            skLineSegment(sketch, "E60.14.5", {"start": v(-48, -22.15) * mm, "end": v(-43.66, -7.37) * mm});
            skLineSegment(sketch, "E60.15.0", {"start": v(-43.1, -7.51) * mm, "end": v(-46.98, -25.7) * mm});
            skLineSegment(sketch, "E60.15.1", {"start": v(-46.98, -25.7) * mm, "end": v(-44.84, -26.07) * mm, "construction": true});
            skLineSegment(sketch, "E60.15.2", {"start": v(-44.84, -26.07) * mm, "end": v(-42.47, -7.62) * mm});
            skLineSegment(sketch, "E60.15.3", {"start": v(-42.7, -23.05) * mm, "end": v(-41.89, -7.67) * mm});
            skLineSegment(sketch, "E60.15.4", {"start": v(-40.04, -23.04) * mm, "end": v(-42.7, -23.05) * mm});
            skLineSegment(sketch, "E60.15.5", {"start": v(-40.04, -23.04) * mm, "end": v(-41, -7.67) * mm});
            skLineSegment(sketch, "E60.16.0", {"start": v(-40.43, -7.6) * mm, "end": v(-37.86, -26.03) * mm});
            skLineSegment(sketch, "E60.16.1", {"start": v(-37.86, -26.03) * mm, "end": v(-35.73, -25.64) * mm, "construction": true});
            skLineSegment(sketch, "E60.16.2", {"start": v(-35.73, -25.64) * mm, "end": v(-39.8, -7.5) * mm});
            skLineSegment(sketch, "E60.16.3", {"start": v(-34.74, -22.08) * mm, "end": v(-39.24, -7.35) * mm});
            skLineSegment(sketch, "E60.16.4", {"start": v(-32.24, -21.15) * mm, "end": v(-34.74, -22.08) * mm});
            skLineSegment(sketch, "E60.16.5", {"start": v(-32.24, -21.15) * mm, "end": v(-38.41, -7.04) * mm});
            skLineSegment(sketch, "E60.17.0", {"start": v(-37.89, -6.79) * mm, "end": v(-29.18, -23.22) * mm});
            skLineSegment(sketch, "E60.17.1", {"start": v(-29.18, -23.22) * mm, "end": v(-27.3, -22.13) * mm, "construction": true});
            skLineSegment(sketch, "E60.17.2", {"start": v(-27.3, -22.13) * mm, "end": v(-37.34, -6.47) * mm});
            skLineSegment(sketch, "E60.17.3", {"start": v(-27.6, -18.44) * mm, "end": v(-36.86, -6.14) * mm});
            skLineSegment(sketch, "E60.17.4", {"start": v(-25.57, -16.72) * mm, "end": v(-27.6, -18.44) * mm});
            skLineSegment(sketch, "E60.17.5", {"start": v(-25.57, -16.72) * mm, "end": v(-36.19, -5.56) * mm});
            skArc(sketch, "E61", {"start": v(-45.09, 6.79) * mm, "mid": v(-45.36, 6.63) * mm, "end": v(-45.63, 6.47) * mm});
            skArc(sketch, "E62.trimOffspring", {"start": v(-46.11, 6.14) * mm, "mid": v(-46.46, 5.86) * mm, "end": v(-46.79, 5.56) * mm});
            skArc(sketch, "E63.trimOffspring", {"start": v(-47.2, 5.15) * mm, "mid": v(-47.4, 4.9) * mm, "end": v(-47.6, 4.66) * mm});
            skArc(sketch, "E64.trimOffspring", {"start": v(-47.93, 4.18) * mm, "mid": v(-48.16, 3.8) * mm, "end": v(-48.37, 3.42) * mm});
            skArc(sketch, "E65.trimOffspring", {"start": v(-48.6, 2.89) * mm, "mid": v(-48.72, 2.6) * mm, "end": v(-48.82, 2.29) * mm});
            skArc(sketch, "E66.trimOffspring", {"start": v(-48.97, 1.73) * mm, "mid": v(-49.06, 1.3) * mm, "end": v(-49.12, 0.86) * mm});
            skArc(sketch, "E67.trimOffspring", {"start": v(-43.73, 7.35) * mm, "mid": v(-44.15, 7.2) * mm, "end": v(-44.56, 7.04) * mm});
            skArc(sketch, "E68.trimOffspring", {"start": v(-42.55, 7.6) * mm, "mid": v(-42.86, 7.56) * mm, "end": v(-43.17, 7.5) * mm});
            skArc(sketch, "E69.trimOffspring", {"start": v(-41.08, 7.67) * mm, "mid": v(-41.53, 7.68) * mm, "end": v(-41.97, 7.67) * mm});
            skArc(sketch, "E70.trimOffspring", {"start": v(-39.88, 7.51) * mm, "mid": v(-40.2, 7.57) * mm, "end": v(-40.5, 7.62) * mm});
            skArc(sketch, "E71.trimOffspring", {"start": v(-38.48, 7.07) * mm, "mid": v(-38.9, 7.23) * mm, "end": v(-39.32, 7.37) * mm});
            skArc(sketch, "E72.trimOffspring", {"start": v(-37.4, 6.51) * mm, "mid": v(-37.68, 6.67) * mm, "end": v(-37.96, 6.83) * mm});
            skArc(sketch, "E73.trimOffspring", {"start": v(-36.25, 5.62) * mm, "mid": v(-36.58, 5.91) * mm, "end": v(-36.93, 6.18) * mm});
            skArc(sketch, "E74.trimOffspring", {"start": v(-35.43, 4.72) * mm, "mid": v(-35.63, 4.97) * mm, "end": v(-35.84, 5.2) * mm});
            skArc(sketch, "E75.trimOffspring", {"start": v(-34.64, 3.49) * mm, "mid": v(-34.85, 3.88) * mm, "end": v(-35.09, 4.25) * mm});
            skArc(sketch, "E76.trimOffspring", {"start": v(-34.18, 2.37) * mm, "mid": v(-34.28, 2.67) * mm, "end": v(-34.4, 2.96) * mm});
            skArc(sketch, "E77.trimOffspring", {"start": v(-33.86, 0.94) * mm, "mid": v(-33.93, 1.37) * mm, "end": v(-34.02, 1.8) * mm});
            skArc(sketch, "E78.trimOffspring", {"start": v(-33.8, -0.28) * mm, "mid": v(-33.8, 0.04) * mm, "end": v(-33.81, 0.36) * mm});
            skArc(sketch, "E79.trimOffspring", {"start": v(-49.11, -0.94) * mm, "mid": v(-48.91, -1.97) * mm, "end": v(-48.58, -2.96) * mm});
            skArc(sketch, "E80.trimOffspring", {"start": v(-48.33, -3.49) * mm, "mid": v(-48.12, -3.88) * mm, "end": v(-47.89, -4.25) * mm});
            skArc(sketch, "E81.trimOffspring", {"start": v(-47.55, -4.72) * mm, "mid": v(-47.35, -4.97) * mm, "end": v(-47.14, -5.2) * mm});
            skArc(sketch, "E82.trimOffspring", {"start": v(-46.73, -5.62) * mm, "mid": v(-46.4, -5.91) * mm, "end": v(-46.05, -6.18) * mm});
            skArc(sketch, "E83.trimOffspring", {"start": v(-45.57, -6.51) * mm, "mid": v(-45.3, -6.67) * mm, "end": v(-45.01, -6.83) * mm});
            skArc(sketch, "E84.trimOffspring", {"start": v(-44.49, -7.07) * mm, "mid": v(-44.08, -7.23) * mm, "end": v(-43.66, -7.37) * mm});
            skArc(sketch, "E85.trimOffspring", {"start": v(-43.1, -7.51) * mm, "mid": v(-42.78, -7.57) * mm, "end": v(-42.47, -7.62) * mm});
            skArc(sketch, "E86.trimOffspring", {"start": v(-41.89, -7.67) * mm, "mid": v(-41.45, -7.68) * mm, "end": v(-41, -7.67) * mm});
            skArc(sketch, "E87.trimOffspring", {"start": v(-40.43, -7.6) * mm, "mid": v(-40.11, -7.56) * mm, "end": v(-39.8, -7.5) * mm});
            skArc(sketch, "E88.trimOffspring", {"start": v(-39.24, -7.35) * mm, "mid": v(-38.82, -7.2) * mm, "end": v(-38.41, -7.04) * mm});
            skArc(sketch, "E89.trimOffspring", {"start": v(-37.89, -6.79) * mm, "mid": v(-37.61, -6.63) * mm, "end": v(-37.34, -6.47) * mm});
            skArc(sketch, "E90.trimOffspring", {"start": v(-36.86, -6.14) * mm, "mid": v(-36.52, -5.86) * mm, "end": v(-36.19, -5.56) * mm});
            skArc(sketch, "E91.trimOffspring", {"start": v(-35.78, -5.15) * mm, "mid": v(-35.58, -4.9) * mm, "end": v(-35.38, -4.66) * mm});
            skArc(sketch, "E92.trimOffspring", {"start": v(-35.04, -4.18) * mm, "mid": v(-34.81, -3.8) * mm, "end": v(-34.6, -3.42) * mm});
            skArc(sketch, "E93.trimOffspring", {"start": v(-34.37, -2.89) * mm, "mid": v(-34.27, -2.64) * mm, "end": v(-34.18, -2.38) * mm});
            skLineSegment(sketch, "E94", {"start": v(-19.45, -6.88) * mm, "end": v(-34.18, -2.38) * mm});
            skArc(sketch, "E95.trimOffspring", {"start": v(-34, -1.73) * mm, "mid": v(-33.91, -1.3) * mm, "end": v(-33.85, -0.86) * mm});
            skLineSegment(sketch, "E96", {"start": v(-62.22, -16.16) * mm, "end": v(-60.81, -17.81) * mm});
            skLineSegment(sketch, "E97", {"start": v(-65.74, -10.13) * mm, "end": v(-66.5, -8.1) * mm});
            skLineSegment(sketch, "E98", {"start": v(-67.74, -1.22) * mm, "end": v(-67.75, 0.95) * mm});
            skLineSegment(sketch, "E99", {"start": v(-66.57, 7.83) * mm, "end": v(-65.84, 9.87) * mm});
            skLineSegment(sketch, "E100", {"start": v(-37.86, -26.03) * mm, "end": v(-35.73, -25.64) * mm});
            skLineSegment(sketch, "E101", {"start": v(-29.18, -23.22) * mm, "end": v(-27.3, -22.13) * mm});
            skLineSegment(sketch, "E102", {"start": v(-21.98, -17.6) * mm, "end": v(-20.6, -15.94) * mm});
            skLineSegment(sketch, "E103", {"start": v(-46.98, -25.7) * mm, "end": v(-44.84, -26.07) * mm});
            skLineSegment(sketch, "E104", {"start": v(-53.56, -23.35) * mm, "end": v(-55.44, -22.27) * mm});
            skLineSegment(sketch, "E105", {"start": v(-62.38, 15.94) * mm, "end": v(-61, 17.6) * mm});
            skLineSegment(sketch, "E106", {"start": v(-55.67, 22.13) * mm, "end": v(-53.8, 23.22) * mm});
            skLineSegment(sketch, "E107", {"start": v(-47.25, 25.64) * mm, "end": v(-45.11, 26.03) * mm});
            skLineSegment(sketch, "E108", {"start": v(-38.13, 26.07) * mm, "end": v(-36, 25.7) * mm});
            skLineSegment(sketch, "E109", {"start": v(-29.42, 23.35) * mm, "end": v(-27.53, 22.27) * mm});
            skLineSegment(sketch, "E110", {"start": v(-22.16, 17.81) * mm, "end": v(-20.76, 16.16) * mm});
            skLineSegment(sketch, "E111", {"start": v(-17.23, 10.13) * mm, "end": v(-16.48, 8.1) * mm});
            skLineSegment(sketch, "E112", {"start": v(-15.23, 1.22) * mm, "end": v(-15.22, -0.95) * mm});
            skLineSegment(sketch, "E113", {"start": v(-16.4, -7.83) * mm, "end": v(-17.13, -9.87) * mm});
            skLineSegment(sketch, "E114", {"start": v(-49.16, -0.36) * mm, "end": v(-49.17, 0.28) * mm});
            skSolve(sketch);
        }
        {
            var Q0;
            Q0=qSketchRegion(id+"F9",true);
            extrude(context, id + "F10", {"entities" : qUnion([Q0]), "operationType" : NewBodyOperationType.REMOVE, "depth" : 4.5 * mm});
        }
        {
            var Q0;
            Q0=makeQuery(id+"F0.imprint","IMPRINT",FACE,{"disambiguationData":[TD([[makeQuery(id+"F0.imprint","IMPRINT",EDGE,{"derivedFrom":sQuery(id+"F0.wireOp",EDGE,"E0")}),-1.0]])]});
            var sketch = newSketch(context, id + "F11", { "sketchPlane" : qUnion([Q0])});
            skCircle(sketch, "E115", {"center": v(-41.49, 0) * mm, "radius": 5.37 * mm});
            skCircle(sketch, "E116", {"center": v(-41.49, 0) * mm, "radius": 7.09 * mm});
            skLineSegment(sketch, "E117.bottom", {"start": v(-41.49, 0) * mm, "end": v(-41.49, 0) * mm});
            skSolve(sketch);
        }
        {
            var Q0;
            Q0=qSketchRegion(id+"F11",true);
            var Q1;
            Q1=makeQuery(id+"F10.boolean.opBoolean","COPY",FACE,{"derivedFrom":makeQuery(id+"F10.opExtrude","CAP_FACE",FACE,{"disambiguationData":[OSD([sQuery(id+"F9.wireOp",EDGE,"E60.11.3"),sQuery(id+"F9.wireOp",EDGE,"E60.11.4"),sQuery(id+"F9.wireOp",EDGE,"E60.11.5"),sQuery(id+"F9.wireOp",EDGE,"E79.trimOffspring")])],"isStart":false})});
            extrude(context, id + "F12", {"entities" : qUnion([Q0]), "operationType" : NewBodyOperationType.REMOVE, "endBound" : BoundingType.UP_TO_SURFACE, "endBoundEntityFace" : qUnion([Q1]), "depth" : 25 * mm});
        }
        {
            var Q0;
            {var subQ0=sQuery(id+"F0.wireOp",EDGE,"E36");var subQ1=sQuery(id+"F0.wireOp",EDGE,"E35");var subQ2=sQuery(id+"F0.wireOp",EDGE,"E34");var subQ3=sQuery(id+"F0.wireOp",EDGE,"E33");var subQ4=sQuery(id+"F0.wireOp",EDGE,"E32");var subQ5=sQuery(id+"F0.wireOp",EDGE,"E31");var subQ6=sQuery(id+"F0.wireOp",EDGE,"E30");var subQ7=sQuery(id+"F0.wireOp",EDGE,"E29");var subQ8=sQuery(id+"F0.wireOp",EDGE,"E28");var subQ9=sQuery(id+"F0.wireOp",EDGE,"E27");var subQ10=sQuery(id+"F0.wireOp",EDGE,"E26");var subQ11=sQuery(id+"F0.wireOp",EDGE,"E25");var subQ12=sQuery(id+"F0.wireOp",EDGE,"E24");var subQ13=sQuery(id+"F0.wireOp",EDGE,"E23");var subQ14=sQuery(id+"F0.wireOp",EDGE,"E22");var subQ15=sQuery(id+"F0.wireOp",EDGE,"E21");var subQ16=sQuery(id+"F0.wireOp",EDGE,"E20");var subQ17=sQuery(id+"F0.wireOp",EDGE,"E19");var subQ18=sQuery(id+"F0.wireOp",EDGE,"E18");var subQ19=sQuery(id+"F0.wireOp",EDGE,"E17");var subQ20=sQuery(id+"F0.wireOp",EDGE,"E16");var subQ21=sQuery(id+"F0.wireOp",EDGE,"E15");var subQ22=sQuery(id+"F0.wireOp",EDGE,"E14");var subQ23=sQuery(id+"F0.wireOp",EDGE,"E13");var subQ24=sQuery(id+"F0.wireOp",EDGE,"E12");var subQ25=sQuery(id+"F0.wireOp",EDGE,"E11");var subQ26=sQuery(id+"F0.wireOp",EDGE,"E10");var subQ27=sQuery(id+"F0.wireOp",EDGE,"E9");var subQ28=sQuery(id+"F0.wireOp",EDGE,"E8");var subQ29=sQuery(id+"F0.wireOp",EDGE,"E7");var subQ30=sQuery(id+"F0.wireOp",EDGE,"E6");var subQ31=sQuery(id+"F0.wireOp",EDGE,"E5");var subQ32=sQuery(id+"F0.wireOp",EDGE,"E4");var subQ33=sQuery(id+"F0.wireOp",EDGE,"E3");var subQ34=sQuery(id+"F0.wireOp",EDGE,"E1");var subQ35=sQuery(id+"F0.wireOp",EDGE,"E0");Q0=makeQuery(id+"F5.boolean.opBoolean","MERGE",FACE,{"derivedFrom":[makeQuery(id+"F1.opExtrude","CAP_FACE",FACE,{"disambiguationData":[OSD([subQ35,subQ34,subQ33,subQ32,subQ31,subQ30,subQ29,subQ28,subQ27,subQ26,subQ25,subQ24,subQ23,subQ22,subQ21,subQ20,subQ19,subQ18,subQ17,subQ16,subQ15,subQ14,subQ13,subQ12,subQ11,subQ10,subQ9,subQ8,subQ7,subQ6,subQ5,subQ4,subQ3,subQ2,subQ1,subQ0])],"isStart":false}),makeQuery(id+"F5.opExtrude","CAP_FACE",FACE,{"disambiguationData":[OSD([subQ35,subQ34,subQ33,subQ32,subQ31,subQ30,subQ29,subQ28,subQ27,subQ26,subQ25,subQ24,subQ23,subQ22,subQ21,subQ20,subQ19,subQ18,subQ17,subQ16,subQ15,subQ14,subQ13,subQ12,subQ11,subQ10,subQ9,subQ8,subQ7,subQ6,subQ5,subQ4,subQ3,subQ2,subQ1,subQ0])],"isStart":false})]});}
            var sketch = newSketch(context, id + "F13", { "sketchPlane" : qUnion([Q0])});
            skText(sketch, "E118", { "text": "Christiana\n  Aguirre", "fontName": "OpenSans-Bold.ttf"});
            const initialGuessF13  = {"E118": [-0.06386, 0.00296, 1, 0, 0.00638]};
            skSetInitialGuess(sketch, initialGuessF13);
            skSolve(sketch);
        }
        {
            var Q0;
            Q0=qSketchRegion(id+"F13",true);
            extrude(context, id + "F14", {"entities" : qUnion([Q0]), "operationType" : NewBodyOperationType.ADD, "depth" : 3 * mm});
        }
    });
